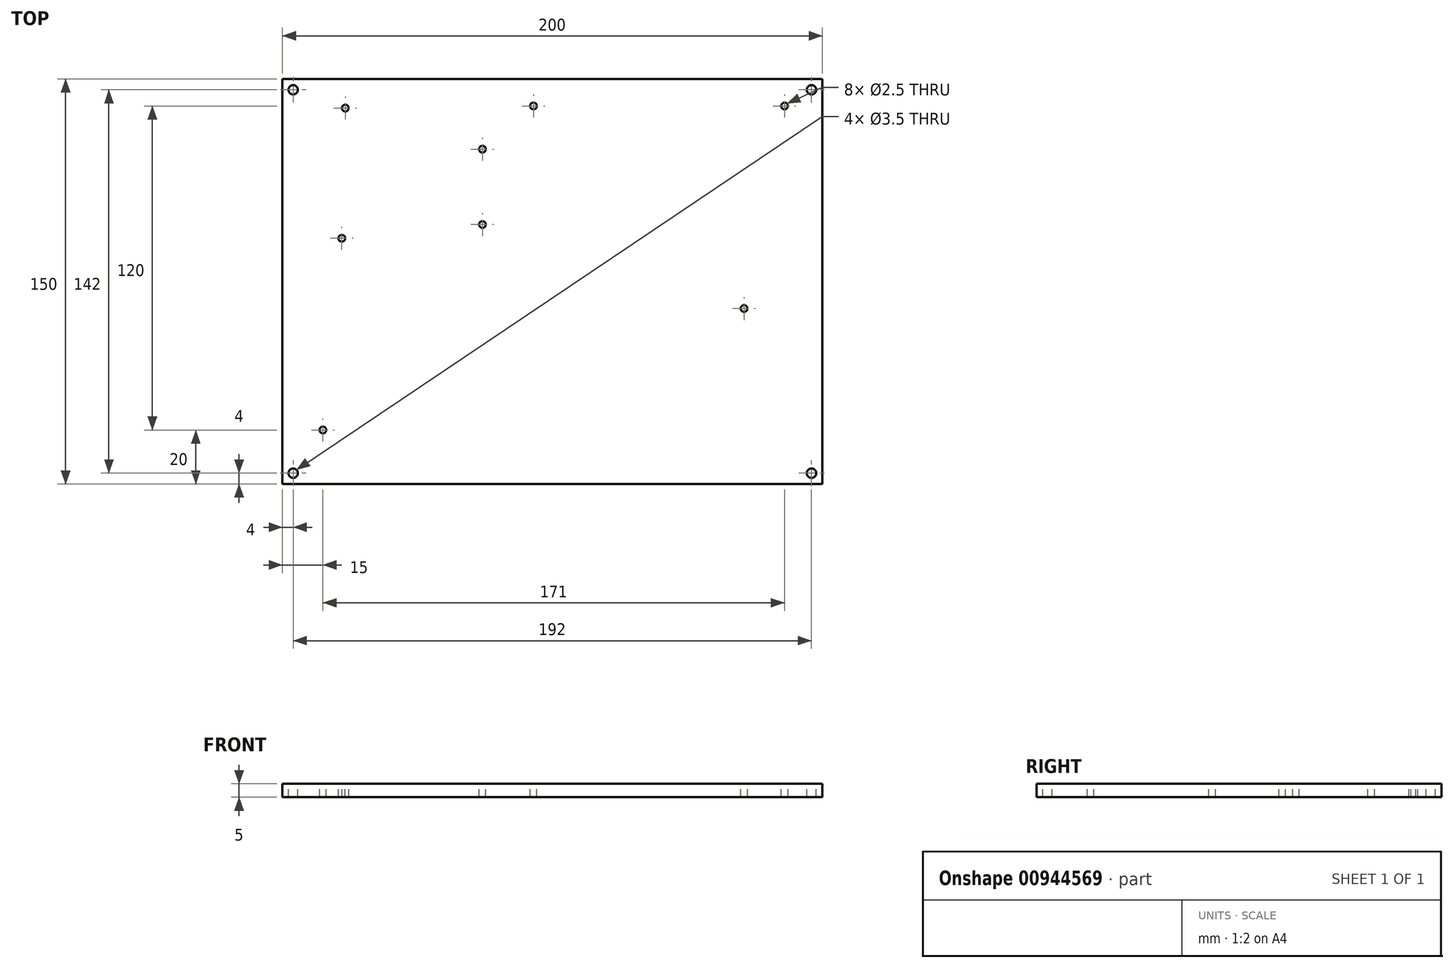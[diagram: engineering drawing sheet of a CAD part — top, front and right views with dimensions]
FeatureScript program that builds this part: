
annotation { "Feature Type Name" : "Feature", "Feature Type Description" : "" }
export const myFeature = defineFeature(function(context is Context, id is Id, definition is map)
    precondition{}
    {
        {
            var Q0;
            Q0=qCreatedBy(makeId("Top.planeOp"),FACE);
            var sketch = newSketch(context, id + "F0", { "sketchPlane" : qUnion([Q0])});
            skLineSegment(sketch, "E0.bottom", {"start": v(100, -75) * mm, "end": v(-100, -75) * mm});
            skLineSegment(sketch, "E0.top", {"start": v(100, 75) * mm, "end": v(-100, 75) * mm});
            skLineSegment(sketch, "E0.left", {"start": v(100, -75) * mm, "end": v(100, 75) * mm});
            skLineSegment(sketch, "E0.right", {"start": v(-100, -75) * mm, "end": v(-100, 75) * mm});
            skPoint(sketch, "E0.middle", {"position": v(0, 0) * mm});
            skCircle(sketch, "E1", {"center": v(-96, 71) * mm, "radius": 1.6 * mm});
            skCircle(sketch, "E2.0.1.0", {"center": v(-96, -71) * mm, "radius": 1.6 * mm});
            skCircle(sketch, "E2.1.0.0", {"center": v(96, 71) * mm, "radius": 1.6 * mm});
            skCircle(sketch, "E2.1.1.0", {"center": v(96, -71) * mm, "radius": 1.6 * mm});
            skCircle(sketch, "E2.2.0.0", {"center": v(288, 71) * mm, "radius": 1.6 * mm});
            skCircle(sketch, "E2.2.1.0", {"center": v(288, -71) * mm, "radius": 1.6 * mm});
            skLineSegment(sketch, "E2.direction1", {"start": v(-96, 71) * mm, "end": v(96, 71) * mm, "construction": true});
            skLineSegment(sketch, "E2.direction2", {"start": v(-96, 71) * mm, "end": v(-96, -71) * mm, "construction": true});
            skSolve(sketch);
        }
        {
            var Q0;
            Q0=makeQuery(id+"F0.imprint","IMPRINT",FACE,{"disambiguationData":[TD([[makeQuery(id+"F0.imprint","IMPRINT",EDGE,{"derivedFrom":sQuery(id+"F0.wireOp",EDGE,"E0.bottom")}),-1.0]])]});
            extrude(context, id + "F1", {"entities" : qUnion([Q0]), "depth" : 5 * mm, "offsetDistance" : 25 * mm});
        }
        {
            var Q0;
            Q0=makeQuery(id+"F1.opExtrude","CAP_FACE",FACE,{"disambiguationData":[OSD([sQuery(id+"F0.wireOp",EDGE,"E0.bottom"),sQuery(id+"F0.wireOp",EDGE,"E0.top"),sQuery(id+"F0.wireOp",EDGE,"E0.left"),sQuery(id+"F0.wireOp",EDGE,"E0.right"),sQuery(id+"F0.wireOp",EDGE,"E1"),sQuery(id+"F0.wireOp",EDGE,"E2.0.1.0"),sQuery(id+"F0.wireOp",EDGE,"E2.1.0.0"),sQuery(id+"F0.wireOp",EDGE,"E2.1.1.0")])],"isStart":false});
            var sketch = newSketch(context, id + "F2", { "sketchPlane" : qUnion([Q0])});
            skPoint(sketch, "E3", {"position": v(-76.7, 64.2) * mm});
            skPoint(sketch, "E4", {"position": v(-25.9, 49) * mm});
            skPoint(sketch, "E5", {"position": v(-25.9, 21.1) * mm});
            skPoint(sketch, "E6", {"position": v(-78, 16) * mm});
            skPoint(sketch, "E7", {"position": v(-85, -55) * mm});
            skPoint(sketch, "E8", {"position": v(71, -10) * mm});
            skPoint(sketch, "E9", {"position": v(-7, 65) * mm});
            skPoint(sketch, "E10", {"position": v(86, 65) * mm});
            skSolve(sketch);
        }
        {
            var Q0;
            Q0=sQuery(id+"F2.wireOp",VERTEX,"E3");
            var Q1;
            Q1=sQuery(id+"F2.wireOp",VERTEX,"E4");
            var Q2;
            Q2=sQuery(id+"F2.wireOp",VERTEX,"E5");
            var Q3;
            Q3=sQuery(id+"F2.wireOp",VERTEX,"E6");
            var Q4;
            Q4=sQuery(id+"F2.wireOp",VERTEX,"E7");
            var Q5;
            Q5=sQuery(id+"F2.wireOp",VERTEX,"E8");
            var Q6;
            Q6=sQuery(id+"F2.wireOp",VERTEX,"E9");
            var Q7;
            Q7=sQuery(id+"F2.wireOp",VERTEX,"E10");
            var Q8;
            Q8=makeQuery(id+"F1.opExtrude","SWEPT_BODY",BODY,{"disambiguationData":[OSD([sQuery(id+"F0.wireOp",EDGE,"E0.bottom"),sQuery(id+"F0.wireOp",EDGE,"E0.top"),sQuery(id+"F0.wireOp",EDGE,"E0.left"),sQuery(id+"F0.wireOp",EDGE,"E0.right"),sQuery(id+"F0.wireOp",EDGE,"E1"),sQuery(id+"F0.wireOp",EDGE,"E2.0.1.0"),sQuery(id+"F0.wireOp",EDGE,"E2.1.0.0"),sQuery(id+"F0.wireOp",EDGE,"E2.1.1.0")])]});
            hole(context, id + "F3", {"style" : HoleStyle.SIMPLE, "endStyle" : HoleEndStyle.THROUGH, "standardTappedOrClearance" : lookupTablePath({ "standard" : "ISO", "engagement" : "75%", "pitch" : "0.5 mm", "size" : "M3", "type" : "Tapped" }), "standardBlindInLast" : lookupTablePath({ "standard" : "ISO", "fit" : "Normal", "engagement" : "75%", "pitch" : "0.5 mm", "size" : "M3", "type" : "Clearance & tapped" }), "holeDiameter" : 2.5 * mm, "majorDiameter" : 3 * mm, "showTappedDepth" : true, "isTappedThrough" : true, "tappedDepth" : 12 * mm, "tapClearance" : 3, "locations" : qUnion([Q0, Q1, Q2, Q3, Q4, Q5, Q6, Q7]), "scope" : qUnion([Q8])});
        }
        {
            var Q0;
            Q0=makeQuery(id+"F1.opExtrude","CAP_FACE",FACE,{"disambiguationData":[OSD([sQuery(id+"F0.wireOp",EDGE,"E0.bottom"),sQuery(id+"F0.wireOp",EDGE,"E0.top"),sQuery(id+"F0.wireOp",EDGE,"E0.left"),sQuery(id+"F0.wireOp",EDGE,"E0.right"),sQuery(id+"F0.wireOp",EDGE,"E1"),sQuery(id+"F0.wireOp",EDGE,"E2.0.1.0"),sQuery(id+"F0.wireOp",EDGE,"E2.1.0.0"),sQuery(id+"F0.wireOp",EDGE,"E2.1.1.0")])],"isStart":false});
            var sketch = newSketch(context, id + "F4", { "sketchPlane" : qUnion([Q0])});
            skPoint(sketch, "E11", {"position": v(-96, 71) * mm});
            skPoint(sketch, "E12", {"position": v(96, 71) * mm});
            skPoint(sketch, "E13", {"position": v(96, -71) * mm});
            skPoint(sketch, "E14", {"position": v(-96, -71) * mm});
            skSolve(sketch);
        }
        {
            var Q0;
            Q0=sQuery(id+"F4.wireOp",VERTEX,"E14");
            var Q1;
            Q1=sQuery(id+"F4.wireOp",VERTEX,"E11");
            var Q2;
            Q2=sQuery(id+"F4.wireOp",VERTEX,"E12");
            var Q3;
            Q3=sQuery(id+"F4.wireOp",VERTEX,"E13");
            var Q4;
            Q4=makeQuery(id+"F1.opExtrude","SWEPT_BODY",BODY,{"disambiguationData":[OSD([sQuery(id+"F0.wireOp",EDGE,"E0.bottom"),sQuery(id+"F0.wireOp",EDGE,"E0.top"),sQuery(id+"F0.wireOp",EDGE,"E0.left"),sQuery(id+"F0.wireOp",EDGE,"E0.right"),sQuery(id+"F0.wireOp",EDGE,"E1"),sQuery(id+"F0.wireOp",EDGE,"E2.0.1.0"),sQuery(id+"F0.wireOp",EDGE,"E2.1.0.0"),sQuery(id+"F0.wireOp",EDGE,"E2.1.1.0")])]});
            hole(context, id + "F5", {"style" : HoleStyle.SIMPLE, "endStyle" : HoleEndStyle.THROUGH, "standardTappedOrClearance" : lookupTablePath({ "standard" : "ISO", "engagement" : "75%", "pitch" : "0.5 mm", "size" : "M4", "type" : "Tapped" }), "standardBlindInLast" : lookupTablePath({ "standard" : "ISO", "fit" : "Normal", "engagement" : "75%", "pitch" : "0.5 mm", "size" : "M4", "type" : "Clearance & tapped" }), "holeDiameter" : 3.5 * mm, "majorDiameter" : 4 * mm, "showTappedDepth" : true, "isTappedThrough" : true, "tappedDepth" : 1.5 * mm, "tapClearance" : 3, "locations" : qUnion([Q0, Q1, Q2, Q3]), "scope" : qUnion([Q4])});
        }
    });
